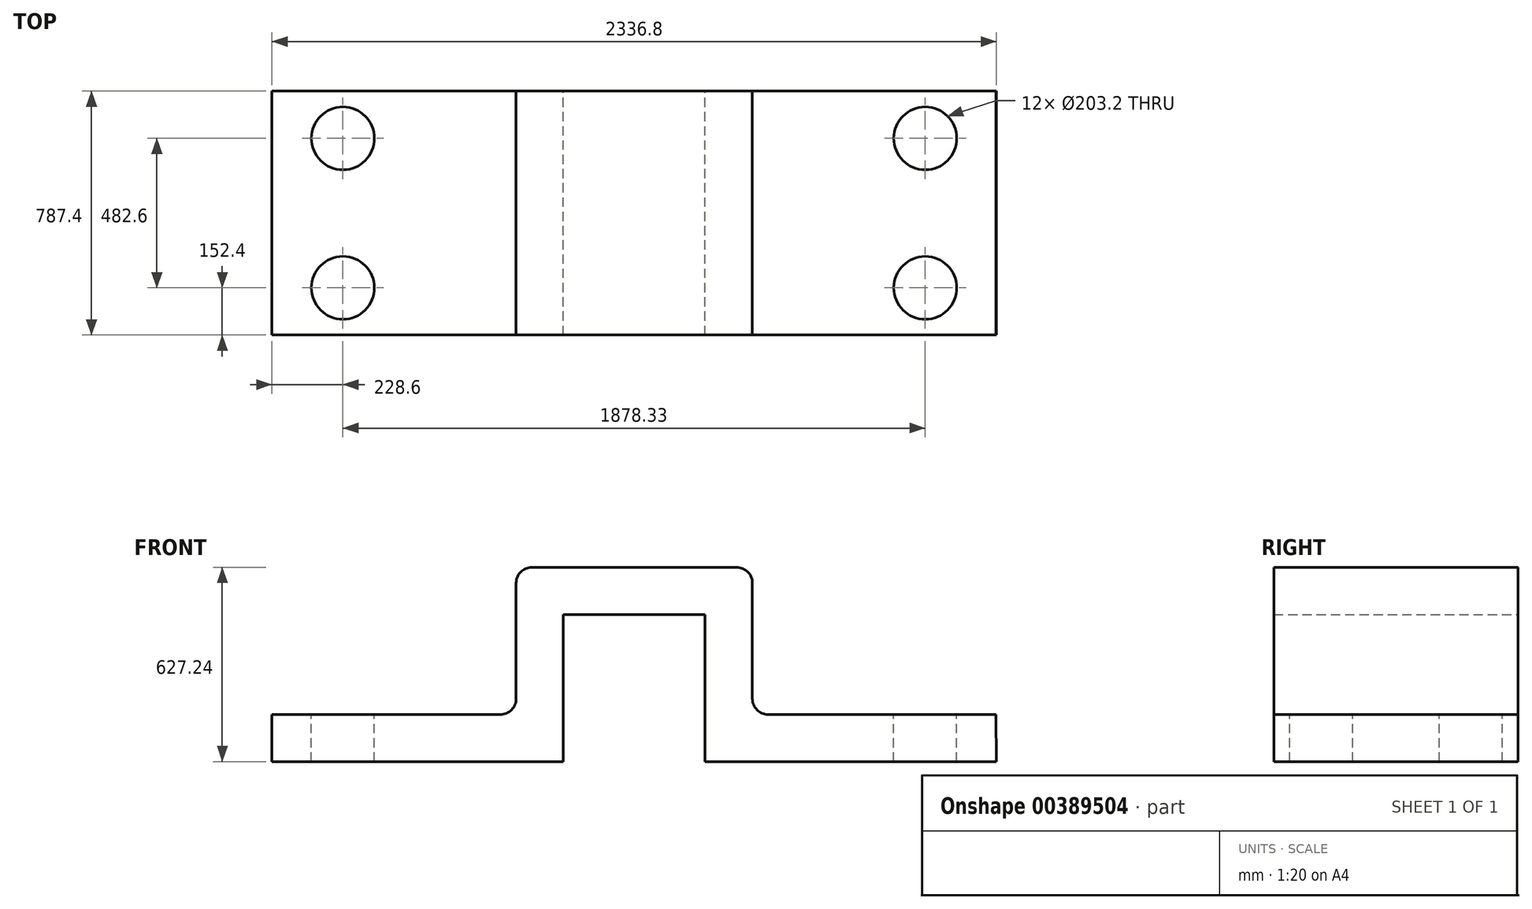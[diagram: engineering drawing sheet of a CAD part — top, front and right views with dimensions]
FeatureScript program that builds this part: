
annotation { "Feature Type Name" : "Feature", "Feature Type Description" : "" }
export const myFeature = defineFeature(function(context is Context, id is Id, definition is map)
    precondition{}
    {
        {
            var Q0;
            Q0=qCreatedBy(makeId("Front.planeOp"),FACE);
            var sketch = newSketch(context, id + "F0", { "sketchPlane" : qUnion([Q0])});
            skLineSegment(sketch, "E0", {"start": v(0, 0) * mm, "end": v(939.8, 0) * mm});
            skLineSegment(sketch, "E1", {"start": v(939.8, 0) * mm, "end": v(939.8, 474.84) * mm});
            skLineSegment(sketch, "E2", {"start": v(939.8, 474.84) * mm, "end": v(1397, 474.84) * mm});
            skLineSegment(sketch, "E3", {"start": v(1397, 474.84) * mm, "end": v(1397, 0) * mm});
            skLineSegment(sketch, "E4", {"start": v(1397, 0) * mm, "end": v(2336.8, 0) * mm});
            skLineSegment(sketch, "E5", {"start": v(0, 152.4) * mm, "end": v(736.6, 152.4) * mm});
            skLineSegment(sketch, "E6", {"start": v(787.4, 203.2) * mm, "end": v(787.4, 576.44) * mm});
            skLineSegment(sketch, "E7", {"start": v(838.2, 627.24) * mm, "end": v(1498.6, 627.24) * mm});
            skLineSegment(sketch, "E8", {"start": v(1549.4, 576.44) * mm, "end": v(1549.4, 203.2) * mm});
            skLineSegment(sketch, "E9", {"start": v(1600.2, 152.4) * mm, "end": v(2335.52, 152.4) * mm});
            skLineSegment(sketch, "E10", {"start": v(2335.52, 152.4) * mm, "end": v(2336.8, 0) * mm});
            skLineSegment(sketch, "E11", {"start": v(0, 152.4) * mm, "end": v(0, 0) * mm});
            skPoint(sketch, "E12.visualSharp", {"position": v(1549.4, 627.24) * mm});
            skArc(sketch, "E12.filletArc", {"start": v(1549.4, 576.44) * mm, "mid": v(1534.52, 612.36) * mm, "end": v(1498.6, 627.24) * mm});
            skPoint(sketch, "E13.visualSharp", {"position": v(787.4, 627.24) * mm});
            skArc(sketch, "E13.filletArc", {"start": v(838.2, 627.24) * mm, "mid": v(802.28, 612.36) * mm, "end": v(787.4, 576.44) * mm});
            skPoint(sketch, "E14.visualSharp", {"position": v(1549.4, 152.4) * mm});
            skArc(sketch, "E14.filletArc", {"start": v(1549.4, 203.2) * mm, "mid": v(1564.28, 167.28) * mm, "end": v(1600.2, 152.4) * mm});
            skPoint(sketch, "E15.visualSharp", {"position": v(787.4, 152.4) * mm});
            skArc(sketch, "E15.filletArc", {"start": v(736.6, 152.4) * mm, "mid": v(772.52, 167.28) * mm, "end": v(787.4, 203.2) * mm});
            skSolve(sketch);
        }
        {
            var Q0;
            Q0=makeQuery(id+"F0.imprint","IMPRINT",FACE,{"disambiguationData":[TD([[makeQuery(id+"F0.imprint","IMPRINT",EDGE,{"derivedFrom":sQuery(id+"F0.wireOp",EDGE,"E0")}),1.0]])]});
            extrude(context, id + "F1", {"entities" : qUnion([Q0]), "depth" : 787.4 * mm});
        }
        {
            var Q0;
            Q0=makeQuery(id+"F1.opExtrude","SWEPT_FACE",FACE,{"disambiguationData":[OSD([sQuery(id+"F0.wireOp",EDGE,"E5")])]});
            var sketch = newSketch(context, id + "F2", { "sketchPlane" : qUnion([Q0])});
            skCircle(sketch, "E16", {"center": v(228.6, -152.4) * mm, "radius": 101.6 * mm});
            skCircle(sketch, "E17", {"center": v(228.6, -635) * mm, "radius": 101.6 * mm});
            skCircle(sketch, "E18", {"center": v(2106.92, -152.4) * mm, "radius": 101.6 * mm});
            skCircle(sketch, "E19", {"center": v(2106.92, -635) * mm, "radius": 101.6 * mm});
            skSolve(sketch);
        }
        {
            var Q0;
            Q0=makeQuery(id+"F2.imprint","IMPRINT",FACE,{"disambiguationData":[TD([[makeQuery(id+"F2.imprint","IMPRINT",EDGE,{"derivedFrom":sQuery(id+"F2.wireOp",EDGE,"E17")}),1.0]])]});
            var Q1;
            Q1=makeQuery(id+"F2.imprint","IMPRINT",FACE,{"disambiguationData":[TD([[makeQuery(id+"F2.imprint","IMPRINT",EDGE,{"derivedFrom":sQuery(id+"F2.wireOp",EDGE,"E18")}),1.0]])]});
            var Q2;
            Q2=makeQuery(id+"F2.imprint","IMPRINT",FACE,{"disambiguationData":[TD([[makeQuery(id+"F2.imprint","IMPRINT",EDGE,{"derivedFrom":sQuery(id+"F2.wireOp",EDGE,"E19")}),1.0]])]});
            var Q3;
            Q3=makeQuery(id+"F2.imprint","IMPRINT",FACE,{"disambiguationData":[TD([[makeQuery(id+"F2.imprint","IMPRINT",EDGE,{"derivedFrom":sQuery(id+"F2.wireOp",EDGE,"E16")}),1.0]])]});
            extrude(context, id + "F3", {"entities" : qUnion([Q0, Q1, Q2, Q3]), "operationType" : NewBodyOperationType.REMOVE, "endBound" : BoundingType.THROUGH_ALL, "oppositeDirection" : true, "depth" : 25.4 * mm});
        }
    });
